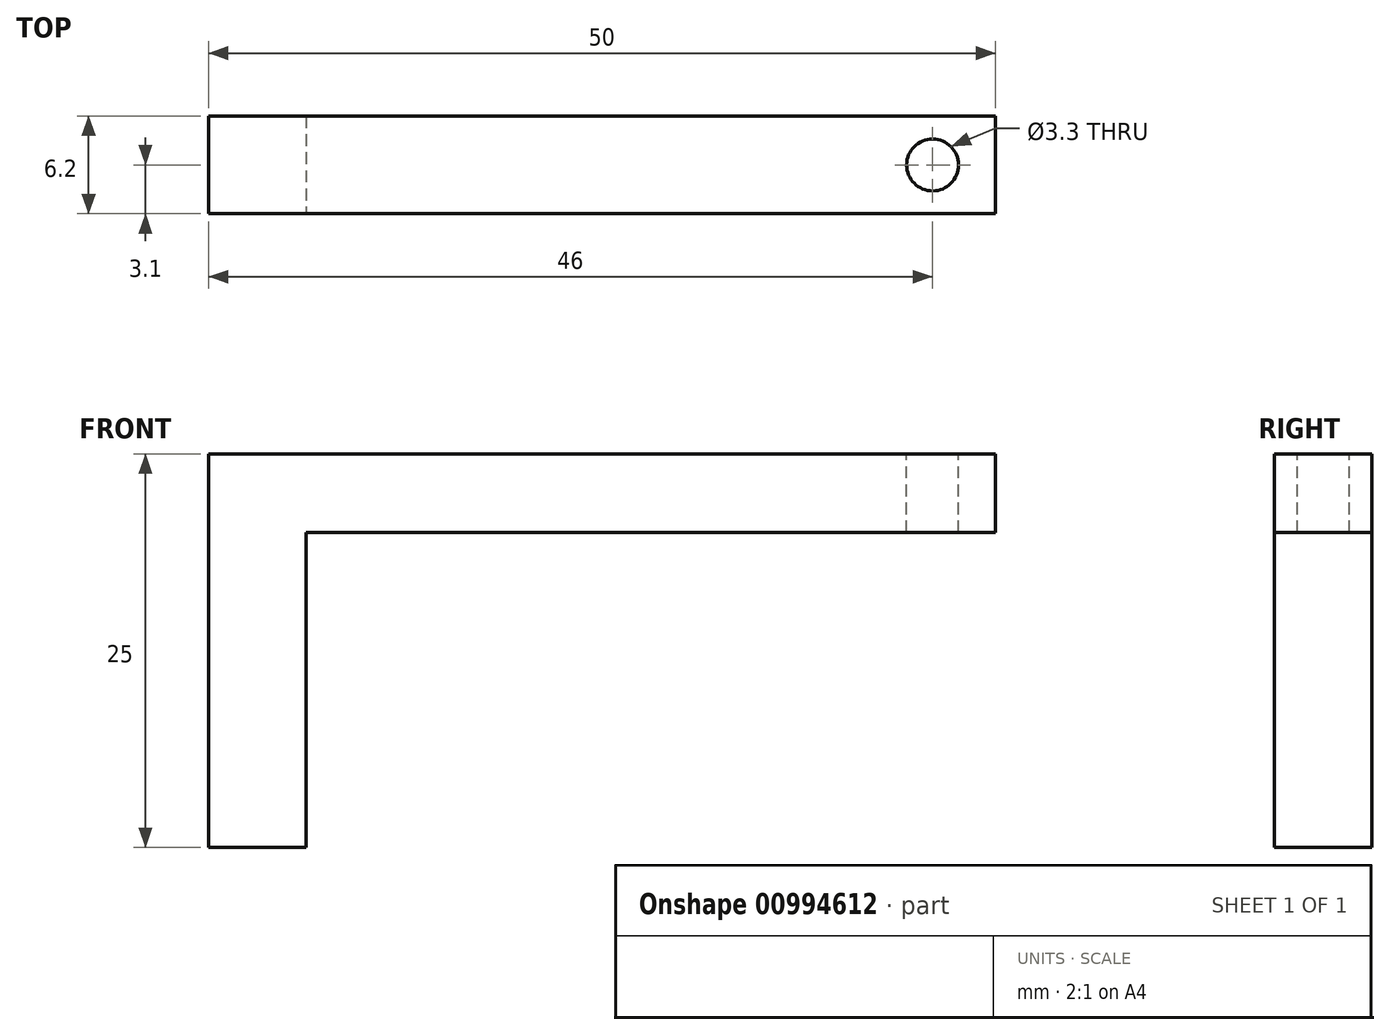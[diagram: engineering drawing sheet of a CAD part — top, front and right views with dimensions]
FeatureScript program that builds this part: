
annotation { "Feature Type Name" : "Feature", "Feature Type Description" : "" }
export const myFeature = defineFeature(function(context is Context, id is Id, definition is map)
    precondition{}
    {
        {
            var Q0;
            Q0=qCreatedBy(makeId("Top.planeOp"),FACE);
            var sketch = newSketch(context, id + "F0", { "sketchPlane" : qUnion([Q0])});
            skLineSegment(sketch, "E0.bottom", {"start": v(-3.1, 3.1) * mm, "end": v(3.1, 3.1) * mm});
            skLineSegment(sketch, "E0.top", {"start": v(-3.1, -3.1) * mm, "end": v(3.1, -3.1) * mm});
            skLineSegment(sketch, "E0.left", {"start": v(-3.1, 3.1) * mm, "end": v(-3.1, -3.1) * mm});
            skLineSegment(sketch, "E0.right", {"start": v(3.1, 3.1) * mm, "end": v(3.1, -3.1) * mm});
            skPoint(sketch, "E0.middle", {"position": v(0, 0) * mm});
            skSolve(sketch);
        }
        {
            var Q0;
            Q0=makeQuery(id+"F0.imprint","IMPRINT",FACE,{"disambiguationData":[TD([[makeQuery(id+"F0.imprint","IMPRINT",EDGE,{"derivedFrom":sQuery(id+"F0.wireOp",EDGE,"E0.bottom")}),-1.0]])]});
            extrude(context, id + "F1", {"entities" : qUnion([Q0]), "depth" : 20 * mm, "offsetDistance" : 25 * mm});
        }
        {
            var Q0;
            Q0=makeQuery(id+"F1.opExtrude","CAP_FACE",FACE,{"disambiguationData":[OSD([sQuery(id+"F0.wireOp",EDGE,"E0.bottom"),sQuery(id+"F0.wireOp",EDGE,"E0.top"),sQuery(id+"F0.wireOp",EDGE,"E0.left"),sQuery(id+"F0.wireOp",EDGE,"E0.right")])],"isStart":false});
            var sketch = newSketch(context, id + "F2", { "sketchPlane" : qUnion([Q0])});
            skLineSegment(sketch, "E1.bottom", {"start": v(-3.1, 3.1) * mm, "end": v(46.9, 3.1) * mm});
            skLineSegment(sketch, "E1.top", {"start": v(-3.1, -3.1) * mm, "end": v(46.9, -3.1) * mm});
            skLineSegment(sketch, "E1.left", {"start": v(-3.1, 3.1) * mm, "end": v(-3.1, -3.1) * mm});
            skLineSegment(sketch, "E1.right", {"start": v(46.9, 3.1) * mm, "end": v(46.9, -3.1) * mm});
            skSolve(sketch);
        }
        {
            var Q0;
            Q0 = qSketchRegion(id + "F2", true);
            extrude(context, id + "F3", {"entities" : qUnion([Q0]), "operationType" : NewBodyOperationType.ADD, "depth" : 5 * mm, "offsetDistance" : 25 * mm});
        }
        {
            var Q0;
            Q0=makeQuery(id+"F3.opExtrude","CAP_FACE",FACE,{"disambiguationData":[OSD([sQuery(id+"F2.wireOp",EDGE,"E1.bottom"),sQuery(id+"F2.wireOp",EDGE,"E1.top"),sQuery(id+"F2.wireOp",EDGE,"E1.left"),sQuery(id+"F2.wireOp",EDGE,"E1.right")])],"isStart":false});
            var sketch = newSketch(context, id + "F4", { "sketchPlane" : qUnion([Q0])});
            skLineSegment(sketch, "E2", {"start": v(46.9, 0) * mm, "end": v(42.9, 0) * mm, "construction": true});
            skCircle(sketch, "E3", {"center": v(42.9, 0) * mm, "radius": 1.65 * mm});
            skSolve(sketch);
        }
        {
            var Q0;
            Q0=makeQuery(id+"F4.imprint","IMPRINT",FACE,{"disambiguationData":[TD([[makeQuery(id+"F4.imprint","IMPRINT",EDGE,{"derivedFrom":sQuery(id+"F4.wireOp",EDGE,"E3")}),1.0]])]});
            extrude(context, id + "F5", {"entities" : qUnion([Q0]), "operationType" : NewBodyOperationType.REMOVE, "oppositeDirection" : true, "depth" : 25 * mm, "offsetDistance" : 25 * mm});
        }
    });
